# Revit family: Haworth_Brazo_Light
name_source: partatom
category: Lighting Fixtures
revit_build: Autodesk Revit 2018 (Build: 20170223_1515(x64)
units: mm (PartAtom-declared; Revit-internal decimal feet)

## family parameters
Always vertical = Yes
Cut with Voids When Loaded = No
Light Source = Yes
OmniClass Number = 23.80.70.11.14
OmniClass Title = General Luminaries, Directional
Part Type = Normal
Room Calculation Point = No
Round Connector Dimension = Use Diameter
Shared = No
Work Plane-Based = No

## types (4) — shared parameters
Actual Width = 26 1/2"
Assembly Code = D5020200
Color Filter = 16777215
Dimming Lamp Color Temperature Shift = <None>
Emit from Line Length = 17"
Glass Finish = Haworth _ Glass _ Clear
Light Source Symbol Size = 17"
Manufacturer = Haworth
Model = LBJ
Revision Number = 6
Size = Verify Final Dim. w/ Haworth
URL = http://www.haworth.com
URL - Product = https://www.haworth.com
Warranty = http://www.haworth.com
Wattage Comments = 1.5 to 9 Watts 120 Volt 60 Hertz

## per-type parameters (varying)
| type | Actual Height | Base | Description | Desk Lamp | Fixed Mount | Floor Lamp | Grommet Mount | Min/Max Height |
| LBJ - Desk Light | 15" | Yes | Haworth Brazo Light - Desk Light | Yes | No | No | No | 14-22 in. |
| LBJ - Floor Light | 50" | Yes | Haworth Brazo Light - Floor Light | No | No | Yes | No | 48-56 in. |
| LBJ - Grommet Mount Light | 15" | No | Haworth Brazo Light - Grommet Mount Light | No | No | No | Yes | 13-21 in. |
| LBJ - Fixed Mount Light | 15" | No | Haworth Brazo Light - Fixed Mount Light | No | Yes | No | No | 13-21 in. |

## geometry (parser evidence)
native form markers: Sweep x3
no freeform markers — native parametric forms only
